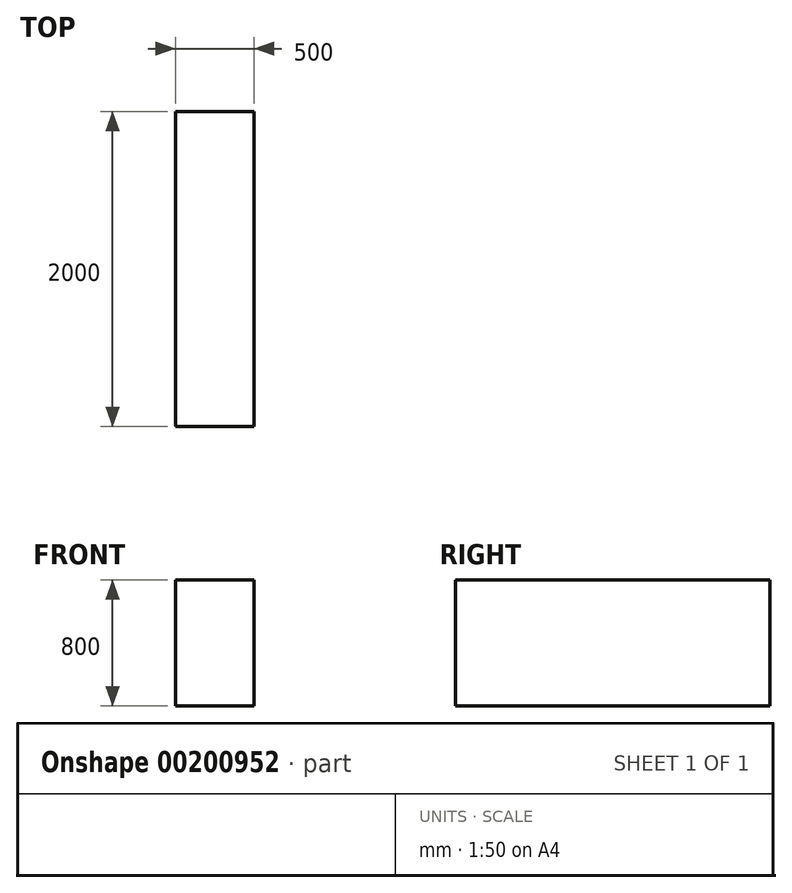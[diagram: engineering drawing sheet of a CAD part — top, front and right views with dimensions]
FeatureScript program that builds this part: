
annotation { "Feature Type Name" : "Feature", "Feature Type Description" : "" }
export const myFeature = defineFeature(function(context is Context, id is Id, definition is map)
    precondition{}
    {
        {
            var Q0;
            Q0=qCreatedBy(makeId("Front.planeOp"),FACE);
            var sketch = newSketch(context, id + "F0", { "sketchPlane" : qUnion([Q0])});
            skLineSegment(sketch, "E0.bottom", {"start": v(250, -400) * mm, "end": v(-250, -400) * mm});
            skLineSegment(sketch, "E0.top", {"start": v(250, 400) * mm, "end": v(-250, 400) * mm});
            skLineSegment(sketch, "E0.left", {"start": v(250, -400) * mm, "end": v(250, 400) * mm});
            skLineSegment(sketch, "E0.right", {"start": v(-250, -400) * mm, "end": v(-250, 400) * mm});
            skPoint(sketch, "E0.middle", {"position": v(0, 0) * mm});
            skSolve(sketch);
        }
        {
            var Q0;
            Q0=makeQuery(id+"F0.imprint","IMPRINT",FACE,{"disambiguationData":[TD([[makeQuery(id+"F0.imprint","IMPRINT",EDGE,{"derivedFrom":sQuery(id+"F0.wireOp",EDGE,"E0.bottom")}),-1.0]])]});
            extrude(context, id + "F1", {"entities" : qUnion([Q0]), "endBound" : BoundingType.SYMMETRIC, "depth" : 2000 * mm});
        }
    });
